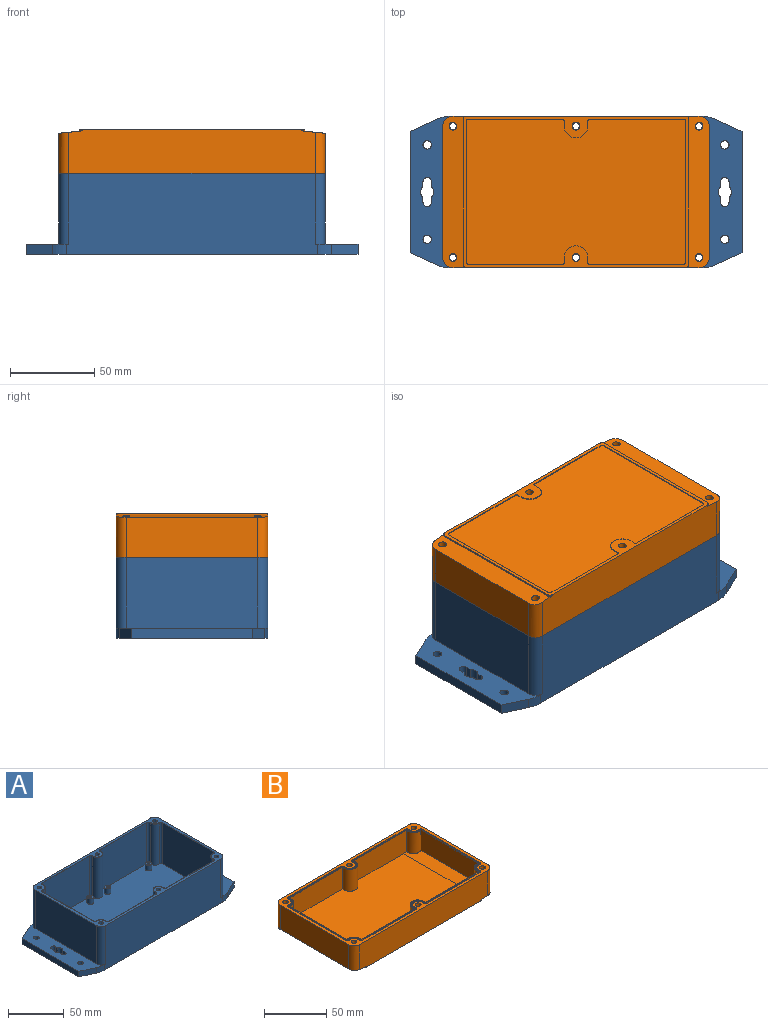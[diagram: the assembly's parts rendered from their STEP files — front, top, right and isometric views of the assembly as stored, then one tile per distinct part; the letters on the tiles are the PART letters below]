
ASSEMBLY  parts=2 mates=1
PART A: 174 faces, bbox 197x90x48.2 mm
  f0: plane 152x84mm, normal (0,0,1), area 12104mm2, adj f98,f99,f100,f101,f102,f103,f104,f106
  f1: plane 158x90mm, normal (0,0,1), area 1628.3mm2, adj f4,f6,f7,f8,f35,f38,f41,f44
  f2: plane 90x25.5mm, normal (0,0,1), area 1458.8mm2, adj f4,f7,f8,f22,f23,f24,f25,f26
  f3: plane 197x90mm, normal (0,0,-1), area 16841.5mm2, adj f7,f8,f9,f10,f11,f12,f13,f14
  f4: plane 78x42mm, normal (1,0,0), area 3276mm2, adj f1,f2,f168,f169
  f5: plane 90x25.5mm, normal (0,0,1), area 1458.8mm2, adj f6,f7,f8,f9,f10,f11,f12,f13
  f6: plane 78x42mm, normal (-1,0,0), area 3276mm2, adj f1,f5,f166,f167
  f7: plane 149.21x48mm, normal (0,-1,0), area 7027.3mm2, adj f1,f2,f3,f5,f167,f168,f171,f173
  f8: plane 149.21x48mm, normal (0,1,0), area 7027.3mm2, adj f1,f2,f3,f5,f166,f169,f170,f172
  f9: plane 15.51x7.16mm, normal (-0.42,0.91,0), area 102.5mm2, adj f3,f5,f10,f172
  f10: plane 72x6mm, normal (-1,0,0), area 432mm2, adj f3,f5,f9,f11
  f11: plane 15.51x7.16mm, normal (-0.42,-0.91,0), area 102.5mm2, adj f3,f5,f10,f173
  f12: cylinder r=2.5mm len=6mm, axis (0,0,1), area 94.2mm2, adj f3,f5
  f13: cylinder r=2.5mm len=6mm, axis (0,0,1), area 94.2mm2, adj f3,f5
  f14: cylinder r=4mm len=6.25mm, axis (0,0,1), area 43mm2, adj f3,f5,f15,f21
  f15: plane 6x3.03mm, normal (1,0,0), area 18.2mm2, adj f3,f5,f14,f16
  f16: cylinder r=2.5mm len=6mm, axis (0,0,1), area 47.1mm2, adj f3,f5,f15,f17
  f17: plane 6x3.03mm, normal (-1,0,0), area 18.2mm2, adj f3,f5,f16,f18
  f18: cylinder r=4mm len=6.25mm, axis (0,0,1), area 43mm2, adj f3,f5,f17,f19
  f19: plane 6x3.03mm, normal (-1,0,0), area 18.2mm2, adj f3,f5,f18,f20
  f20: cylinder r=2.5mm len=6mm, axis (0,0,1), area 47.1mm2, adj f3,f5,f19,f21
  f21: plane 6x3.03mm, normal (1,0,0), area 18.2mm2, adj f3,f5,f14,f20
  f22: plane 15.51x7.16mm, normal (0.42,-0.91,0), area 102.5mm2, adj f2,f3,f23,f171
  f23: plane 72x6mm, normal (1,0,0), area 432mm2, adj f2,f3,f22,f24
  f24: plane 15.51x7.16mm, normal (0.42,0.91,0), area 102.5mm2, adj f2,f3,f23,f170
  f25: cylinder r=2.5mm len=6mm, axis (0,0,1), area 94.2mm2, adj f2,f3
  f26: cylinder r=2.5mm len=6mm, axis (0,0,1), area 94.2mm2, adj f2,f3
  f27: cylinder r=4mm len=6.25mm, axis (0,0,1), area 43mm2, adj f2,f3,f28,f34
  f28: plane 6x3.03mm, normal (-1,0,0), area 18.2mm2, adj f2,f3,f27,f29
  f29: cylinder r=2.5mm len=6mm, axis (0,0,1), area 47.1mm2, adj f2,f3,f28,f30
  f30: plane 6x3.03mm, normal (1,0,0), area 18.2mm2, adj f2,f3,f29,f31
  f31: cylinder r=4mm len=6.25mm, axis (0,0,1), area 43mm2, adj f2,f3,f30,f32
  f32: plane 6x3.03mm, normal (1,0,0), area 18.2mm2, adj f2,f3,f31,f33
  f33: cylinder r=2.5mm len=6mm, axis (0,0,1), area 47.1mm2, adj f2,f3,f32,f34
  f34: plane 6x3.03mm, normal (-1,0,0), area 18.2mm2, adj f2,f3,f27,f33
  f35: cylinder r=2mm len=6mm, axis (0,0,-1), area 75.4mm2, adj f1,f36
  f36: plane 7.5x7.5mm, normal (0,0,-1), area 31.6mm2, adj f35,f37
  f37: cylinder r=3.75mm len=42mm, axis (0,0,-1), area 989.6mm2, adj f3,f36
  f38: cylinder r=2mm len=6mm, axis (0,0,-1), area 75.4mm2, adj f1,f39
  f39: plane 7.5x7.5mm, normal (0,0,-1), area 31.6mm2, adj f38,f40
  f40: cylinder r=3.75mm len=42mm, axis (0,0,-1), area 989.6mm2, adj f3,f39
  f41: cylinder r=2mm len=6mm, axis (0,0,-1), area 75.4mm2, adj f1,f42
  f42: plane 7.5x7.5mm, normal (0,0,-1), area 31.6mm2, adj f41,f43
  f43: cylinder r=3.75mm len=42mm, axis (0,0,-1), area 989.6mm2, adj f3,f42
  f44: cylinder r=2mm len=6mm, axis (0,0,-1), area 75.4mm2, adj f1,f45
  f45: plane 7.5x7.5mm, normal (0,0,-1), area 31.6mm2, adj f44,f46
  f46: cylinder r=3.75mm len=42mm, axis (0,0,-1), area 989.6mm2, adj f3,f45
  f47: cylinder r=2mm len=6mm, axis (0,0,-1), area 75.4mm2, adj f1,f48
  f48: plane 7.5x7.5mm, normal (0,0,-1), area 31.6mm2, adj f47,f49
  f49: cylinder r=3.75mm len=42mm, axis (0,0,-1), area 989.6mm2, adj f3,f48
  f50: cylinder r=2mm len=6mm, axis (0,0,-1), area 75.4mm2, adj f1,f51
  f51: plane 7.5x7.5mm, normal (0,0,-1), area 31.6mm2, adj f50,f52
  f52: cylinder r=3.75mm len=42mm, axis (0,0,-1), area 989.6mm2, adj f3,f51
  f53: plane 152.4x84.4mm, normal (0,0,1), area 95.5mm2, adj f54,f55,f56,f57,f58,f59,f60,f61
  f54: cylinder r=2.2mm len=2.2mm, axis (0,0,-1), area 0.7mm2, adj f1,f53,f55,f85
  f55: plane 59.14x0.2mm, normal (0,1,0), area 11.8mm2, adj f1,f53,f54,f56
  f56: cylinder r=2.2mm len=2.51mm, axis (0,0,-1), area 0.8mm2, adj f1,f53,f55,f57
  f57: cylinder r=4.8mm len=9.6mm, axis (0,0,-1), area 3.3mm2, adj f1,f53,f56,f58
  f58: cylinder r=2.2mm len=2.51mm, axis (0,0,-1), area 0.8mm2, adj f1,f53,f57,f59
  f59: plane 59.14x0.2mm, normal (0,1,0), area 11.8mm2, adj f1,f53,f58,f60
  f60: cylinder r=2.2mm len=2.2mm, axis (0,0,-1), area 0.7mm2, adj f1,f53,f59,f61
  f61: plane 0.93x0.2mm, normal (-1,0,0), area 0.2mm2, adj f1,f53,f60,f62
  f62: cylinder r=4.8mm len=4.8mm, axis (0,0,-1), area 1.5mm2, adj f1,f53,f61,f63
  f63: plane 0.93x0.2mm, normal (0,1,0), area 0.2mm2, adj f1,f53,f62,f64
  f64: cylinder r=2.2mm len=2.2mm, axis (0,0,-1), area 0.7mm2, adj f1,f53,f63,f65
  f65: plane 64.14x0.2mm, normal (-1,0,0), area 12.8mm2, adj f1,f53,f64,f66
  f66: cylinder r=2.2mm len=2.2mm, axis (0,0,-1), area 0.7mm2, adj f1,f53,f65,f67
  f67: plane 0.93x0.2mm, normal (0,-1,0), area 0.2mm2, adj f1,f53,f66,f68
  f68: cylinder r=4.8mm len=4.8mm, axis (0,0,-1), area 1.5mm2, adj f1,f53,f67,f69
  f69: plane 0.93x0.2mm, normal (-1,0,0), area 0.2mm2, adj f1,f53,f68,f70
  f70: cylinder r=2.2mm len=2.2mm, axis (0,0,-1), area 0.7mm2, adj f1,f53,f69,f71
  f71: plane 59.14x0.2mm, normal (0,-1,0), area 11.8mm2, adj f1,f53,f70,f72
  f72: cylinder r=2.2mm len=2.51mm, axis (0,0,-1), area 0.8mm2, adj f1,f53,f71,f73
  f73: cylinder r=4.8mm len=9.6mm, axis (0,0,-1), area 3.3mm2, adj f1,f53,f72,f74
  f74: cylinder r=2.2mm len=2.51mm, axis (0,0,-1), area 0.8mm2, adj f1,f53,f73,f75
  f75: plane 59.14x0.2mm, normal (0,-1,0), area 11.8mm2, adj f1,f53,f74,f76
  f76: cylinder r=2.2mm len=2.2mm, axis (0,0,-1), area 0.7mm2, adj f1,f53,f75,f77
  f77: plane 0.93x0.2mm, normal (1,0,0), area 0.2mm2, adj f1,f53,f76,f78
  f78: cylinder r=4.8mm len=4.8mm, axis (0,0,-1), area 1.5mm2, adj f1,f53,f77,f79
  f79: plane 0.93x0.2mm, normal (0,-1,0), area 0.2mm2, adj f1,f53,f78,f80
  f80: cylinder r=2.2mm len=2.2mm, axis (0,0,-1), area 0.7mm2, adj f1,f53,f79,f81
  f81: plane 64.14x0.2mm, normal (1,0,0), area 12.8mm2, adj f1,f53,f80,f82
  f82: cylinder r=2.2mm len=2.2mm, axis (0,0,-1), area 0.7mm2, adj f1,f53,f81,f83
  f83: plane 0.93x0.2mm, normal (0,1,0), area 0.2mm2, adj f1,f53,f82,f84
  f84: cylinder r=4.8mm len=4.8mm, axis (0,0,-1), area 1.5mm2, adj f1,f53,f83,f85
  f85: plane 0.93x0.2mm, normal (1,0,0), area 0.2mm2, adj f1,f53,f54,f84
  f86: plane 0.93x0.2mm, normal (1,0,0), area 0.2mm2, adj f53,f87,f119,f120
  f87: cylinder r=5mm len=5mm, axis (0,0,-1), area 1.6mm2, adj f53,f86,f88,f120
  f88: plane 0.93x0.2mm, normal (0,-1,0), area 0.2mm2, adj f53,f87,f102,f120
  f89: plane 0.93x0.2mm, normal (0,1,0), area 0.2mm2, adj f53,f90,f116,f117
  f90: cylinder r=5mm len=5mm, axis (0,0,-1), area 1.6mm2, adj f53,f89,f91,f117
  f91: plane 0.93x0.2mm, normal (1,0,0), area 0.2mm2, adj f53,f90,f114,f117
  f92: plane 0.93x0.2mm, normal (-1,0,0), area 0.2mm2, adj f53,f93,f108,f109
  f93: cylinder r=5mm len=5mm, axis (0,0,-1), area 1.6mm2, adj f53,f92,f94,f109
  f94: plane 0.93x0.2mm, normal (0,1,0), area 0.2mm2, adj f53,f93,f106,f109
  f95: plane 0.93x0.2mm, normal (0,-1,0), area 0.2mm2, adj f53,f96,f104,f105
  f96: cylinder r=5mm len=5mm, axis (0,0,-1), area 1.6mm2, adj f53,f95,f97,f105
  f97: plane 0.93x0.2mm, normal (-1,0,0), area 0.2mm2, adj f53,f96,f103,f105
  f98: cylinder r=5mm len=45mm, axis (0,0,-1), area 417.9mm2, adj f0,f114,f116,f117
  f99: cylinder r=5mm len=45mm, axis (0,0,-1), area 417.9mm2, adj f0,f106,f108,f109
  f100: cylinder r=5mm len=45mm, axis (0,0,-1), area 417.9mm2, adj f0,f103,f104,f105
  f101: cylinder r=5mm len=45mm, axis (0,0,-1), area 417.9mm2, adj f0,f102,f119,f120
  f102: cylinder r=2mm len=45.2mm, axis (0,0,-1), area 154.9mm2, adj f0,f53,f88,f101,f118,f120
  f103: cylinder r=2mm len=45.2mm, axis (0,0,-1), area 154.9mm2, adj f0,f53,f97,f100,f105,f125
  f104: cylinder r=2mm len=45.2mm, axis (0,0,-1), area 154.9mm2, adj f0,f53,f95,f100,f105,f107
  f105: plane 6x6mm, normal (0,0,1), area 0.8mm2, adj f95,f96,f97,f100,f103,f104
  f106: cylinder r=2mm len=45.2mm, axis (0,0,-1), area 154.9mm2, adj f0,f53,f94,f99,f107,f109
  f107: plane 64.14x45.2mm, normal (-1,0,0), area 2899.3mm2, adj f0,f53,f104,f106
  f108: cylinder r=2mm len=45.2mm, axis (0,0,-1), area 154.9mm2, adj f0,f53,f92,f99,f109,f113
  f109: plane 6x6mm, normal (0,0,1), area 0.8mm2, adj f92,f93,f94,f99,f106,f108
  f110: cylinder r=2mm len=45.2mm, axis (0,0,-1), area 155mm2, adj f0,f53,f112,f113
  f111: cylinder r=2mm len=45.2mm, axis (0,0,-1), area 155mm2, adj f0,f53,f112,f115
  f112: cylinder r=5mm len=45.2mm, axis (0,0,-1), area 774.8mm2, adj f0,f53,f110,f111
  f113: plane 59.14x45.2mm, normal (0,1,0), area 2673.3mm2, adj f0,f53,f108,f110
  f114: cylinder r=2mm len=45.2mm, axis (0,0,-1), area 154.9mm2, adj f0,f53,f91,f98,f115,f117
  f115: plane 59.14x45.2mm, normal (0,1,0), area 2673.3mm2, adj f0,f53,f111,f114
  f116: cylinder r=2mm len=45.2mm, axis (0,0,-1), area 154.9mm2, adj f0,f53,f89,f98,f117,f118
  f117: plane 6x6mm, normal (0,0,1), area 0.8mm2, adj f89,f90,f91,f98,f114,f116
  f118: plane 64.14x45.2mm, normal (1,0,0), area 2899.3mm2, adj f0,f53,f102,f116
  f119: cylinder r=2mm len=45.2mm, axis (0,0,-1), area 154.9mm2, adj f0,f53,f86,f101,f120,f124
  f120: plane 6x6mm, normal (0,0,1), area 0.8mm2, adj f86,f87,f88,f101,f102,f119
  f121: cylinder r=2mm len=45.2mm, axis (0,0,-1), area 155mm2, adj f0,f53,f123,f125
  f122: cylinder r=2mm len=45.2mm, axis (0,0,-1), area 155mm2, adj f0,f53,f123,f124
  f123: cylinder r=5mm len=45.2mm, axis (0,0,-1), area 774.8mm2, adj f0,f53,f121,f122
  f124: plane 59.14x45.2mm, normal (0,-1,0), area 2673.3mm2, adj f0,f53,f119,f122
  f125: plane 59.14x45.2mm, normal (0,-1,0), area 2673.3mm2, adj f0,f53,f103,f121
  f126: cylinder r=3mm len=6mm, axis (0,0,-1), area 113.1mm2, adj f0,f127
  f127: plane 6x6mm, normal (0,0,1), area 23.4mm2, adj f126,f165
  f128: cylinder r=3mm len=6mm, axis (0,0,-1), area 113.1mm2, adj f0,f129
  f129: plane 6x6mm, normal (0,0,1), area 23.4mm2, adj f128,f163
  f130: cylinder r=3mm len=6mm, axis (0,0,-1), area 113.1mm2, adj f0,f131
  f131: plane 6x6mm, normal (0,0,1), area 23.4mm2, adj f130,f159
  f132: cylinder r=3mm len=6mm, axis (0,0,-1), area 113.1mm2, adj f0,f133
  f133: plane 6x6mm, normal (0,0,1), area 23.4mm2, adj f132,f161
  f134: cylinder r=3mm len=6mm, axis (0,0,-1), area 113.1mm2, adj f0,f135
  f135: plane 6x6mm, normal (0,0,1), area 23.4mm2, adj f134,f149
  f136: cylinder r=3mm len=6mm, axis (0,0,-1), area 113.1mm2, adj f0,f137
  f137: plane 6x6mm, normal (0,0,1), area 23.4mm2, adj f136,f147
  f138: cylinder r=3mm len=6mm, axis (0,0,-1), area 113.1mm2, adj f0,f139
  f139: plane 6x6mm, normal (0,0,1), area 23.4mm2, adj f138,f151
  f140: cylinder r=3mm len=6mm, axis (0,0,-1), area 113.1mm2, adj f0,f141
  f141: plane 6x6mm, normal (0,0,1), area 23.4mm2, adj f140,f153
  f142: cylinder r=3mm len=6mm, axis (0,0,-1), area 113.1mm2, adj f0,f143
  f143: plane 6x6mm, normal (0,0,1), area 23.4mm2, adj f142,f155
  f144: cylinder r=3mm len=6mm, axis (0,0,-1), area 113.1mm2, adj f0,f145
  f145: plane 6x6mm, normal (0,0,1), area 23.4mm2, adj f144,f157
  f146: plane 2.5x2.5mm, normal (0,0,1), area 4.9mm2, adj f147
  f147: cylinder r=1.25mm len=6mm, axis (0,0,1), area 47.1mm2, adj f137,f146
  f148: plane 2.5x2.5mm, normal (0,0,1), area 4.9mm2, adj f149
  f149: cylinder r=1.25mm len=6mm, axis (0,0,1), area 47.1mm2, adj f135,f148
  f150: plane 2.5x2.5mm, normal (0,0,1), area 4.9mm2, adj f151
  f151: cylinder r=1.25mm len=6mm, axis (0,0,1), area 47.1mm2, adj f139,f150
  f152: plane 2.5x2.5mm, normal (0,0,1), area 4.9mm2, adj f153
  f153: cylinder r=1.25mm len=6mm, axis (0,0,1), area 47.1mm2, adj f141,f152
  f154: plane 2.5x2.5mm, normal (0,0,1), area 4.9mm2, adj f155
  f155: cylinder r=1.25mm len=6mm, axis (0,0,1), area 47.1mm2, adj f143,f154
  f156: plane 2.5x2.5mm, normal (0,0,1), area 4.9mm2, adj f157
  f157: cylinder r=1.25mm len=6mm, axis (0,0,1), area 47.1mm2, adj f145,f156
  f158: plane 2.5x2.5mm, normal (0,0,1), area 4.9mm2, adj f159
  f159: cylinder r=1.25mm len=6mm, axis (0,0,1), area 47.1mm2, adj f131,f158
  f160: plane 2.5x2.5mm, normal (0,0,1), area 4.9mm2, adj f161
  f161: cylinder r=1.25mm len=6mm, axis (0,0,1), area 47.1mm2, adj f133,f160
  f162: plane 2.5x2.5mm, normal (0,0,1), area 4.9mm2, adj f163
  f163: cylinder r=1.25mm len=6mm, axis (0,0,1), area 47.1mm2, adj f129,f162
  f164: plane 2.5x2.5mm, normal (0,0,1), area 4.9mm2, adj f165
  f165: cylinder r=1.25mm len=6mm, axis (0,0,1), area 47.1mm2, adj f127,f164
  f166: cylinder r=6mm len=42mm, axis (0,0,-1), area 395.8mm2, adj f1,f5,f6,f8
  f167: cylinder r=6mm len=42mm, axis (0,0,-1), area 395.8mm2, adj f1,f5,f6,f7
  f168: cylinder r=6mm len=42mm, axis (0,0,-1), area 395.8mm2, adj f1,f2,f4,f7
  f169: cylinder r=6mm len=42mm, axis (0,0,-1), area 395.8mm2, adj f1,f2,f4,f8
  f170: cylinder r=20mm len=8.38mm, axis (0,0,-1), area 51.9mm2, adj f2,f3,f8,f24
  f171: cylinder r=20mm len=8.38mm, axis (0,0,-1), area 51.9mm2, adj f2,f3,f7,f22
  f172: cylinder r=20mm len=8.38mm, axis (0,0,1), area 51.9mm2, adj f3,f5,f8,f9
  f173: cylinder r=20mm len=8.38mm, axis (0,0,1), area 51.9mm2, adj f3,f5,f7,f11
PART B: 110 faces, bbox 158.1x90.1x26.1 mm
  f0: plane 158x90mm, normal (0,0,1), area 1469.4mm2, adj f1,f2,f3,f4,f5,f6,f8,f9
  f1: plane 78x23.84mm, normal (-1,0,0), area 1859.4mm2, adj f0,f2,f3,f11
  f2: cylinder r=6mm len=24.47mm, axis (0,0,-1), area 226.8mm2, adj f0,f1,f6,f11
  f3: cylinder r=6mm len=24.47mm, axis (0,0,-1), area 226.8mm2, adj f0,f1,f4,f11
  f4: plane 146x26mm, normal (0,-1,0), area 3778.2mm2, adj f0,f3,f7,f9,f11,f13,f15,f16
  f5: plane 78x23.84mm, normal (1,0,0), area 1859.4mm2, adj f0,f8,f9,f13
  f6: plane 146x26mm, normal (0,1,0), area 3778.2mm2, adj f0,f2,f7,f8,f11,f13,f14,f17
  f7: plane 134x90mm, normal (0,0,-1), area 1111mm2, adj f4,f6,f10,f12,f14,f15,f16,f17
  f8: cylinder r=6mm len=24.47mm, axis (0,0,-1), area 226.8mm2, adj f0,f5,f6,f13
  f9: cylinder r=6mm len=24.47mm, axis (0,0,-1), area 226.8mm2, adj f0,f4,f5,f13
  f10: plane 86x0.9mm, normal (-1,0,0), area 77.4mm2, adj f7,f11,f16,f17
  f11: plane 90.1x14.1mm, normal (-0.1,0,-0.99), area 1038.7mm2, adj f1,f2,f3,f4,f6,f10,f16,f17
  f12: plane 86x0.9mm, normal (1,0,0), area 77.4mm2, adj f7,f13,f14,f15
  f13: plane 90.1x14.1mm, normal (0.1,0,-0.99), area 1038.7mm2, adj f4,f5,f6,f8,f9,f12,f14,f15
  f14: cylinder r=2mm len=2mm, axis (0,0,-1), area 2.5mm2, adj f6,f7,f12,f13
  f15: cylinder r=2mm len=2mm, axis (0,0,-1), area 2.5mm2, adj f4,f7,f12,f13
  f16: cylinder r=2mm len=2mm, axis (0,0,-1), area 2.5mm2, adj f4,f7,f10,f11
  f17: cylinder r=2mm len=2mm, axis (0,0,-1), area 2.5mm2, adj f6,f7,f10,f11
  f18: cylinder r=2.3mm len=24.71mm, axis (0,0,-1), area 353.5mm2, adj f0,f11
  f19: cylinder r=2.3mm len=24.71mm, axis (0,0,-1), area 353.5mm2, adj f0,f11
  f20: cylinder r=2.3mm len=24.71mm, axis (0,0,-1), area 353.5mm2, adj f0,f13
  f21: cylinder r=2.3mm len=24.71mm, axis (0,0,-1), area 353.5mm2, adj f0,f13
  f22: cylinder r=2.3mm len=26mm, axis (0,0,-1), area 375.7mm2, adj f0,f7
  f23: cylinder r=2.3mm len=26mm, axis (0,0,-1), area 375.7mm2, adj f0,f7
  f24: cylinder r=7mm len=14mm, axis (0,0,-1), area 11mm2, adj f7,f25,f43,f44
  f25: plane 3x0.5mm, normal (1,0,0), area 1.5mm2, adj f7,f24,f26,f44
  f26: cylinder r=1mm len=1mm, axis (0,0,-1), area 0.8mm2, adj f7,f25,f27,f44
  f27: plane 56x0.5mm, normal (0,1,0), area 28mm2, adj f7,f26,f28,f44
  f28: cylinder r=1mm len=1mm, axis (0,0,-1), area 0.8mm2, adj f7,f27,f29,f44
  f29: plane 84x0.5mm, normal (-1,0,0), area 42mm2, adj f7,f28,f30,f44
  f30: cylinder r=1mm len=1mm, axis (0,0,-1), area 0.8mm2, adj f7,f29,f31,f44
  f31: plane 56x0.5mm, normal (0,-1,0), area 28mm2, adj f7,f30,f32,f44
  f32: cylinder r=1mm len=1mm, axis (0,0,-1), area 0.8mm2, adj f7,f31,f33,f44
  f33: plane 3x0.5mm, normal (1,0,0), area 1.5mm2, adj f7,f32,f34,f44
  f34: cylinder r=7mm len=14mm, axis (0,0,-1), area 11mm2, adj f7,f33,f35,f44
  f35: plane 3x0.5mm, normal (-1,0,0), area 1.5mm2, adj f7,f34,f36,f44
  f36: cylinder r=1mm len=1mm, axis (0,0,-1), area 0.8mm2, adj f7,f35,f37,f44
  f37: plane 56x0.5mm, normal (0,-1,0), area 28mm2, adj f7,f36,f38,f44
  f38: cylinder r=1mm len=1mm, axis (0,0,-1), area 0.8mm2, adj f7,f37,f39,f44
  f39: plane 84x0.5mm, normal (1,0,0), area 42mm2, adj f7,f38,f40,f44
  f40: cylinder r=1mm len=1mm, axis (0,0,-1), area 0.8mm2, adj f7,f39,f41,f44
  f41: plane 56x0.5mm, normal (0,1,0), area 28mm2, adj f7,f40,f42,f44
  f42: cylinder r=1mm len=1mm, axis (0,0,-1), area 0.8mm2, adj f7,f41,f43,f44
  f43: plane 3x0.5mm, normal (-1,0,0), area 1.5mm2, adj f7,f24,f42,f44
  f44: plane 130x86mm, normal (0,0,-1), area 10912.3mm2, adj f24,f25,f26,f27,f28,f29,f30,f31
  f45: cylinder r=2mm len=2.45mm, axis (0,0,1), area 3.6mm2, adj f0,f46,f68,f69
  f46: cylinder r=4.65mm len=5.7mm, axis (0,0,1), area 9.4mm2, adj f0,f45,f47,f69
  f47: cylinder r=2mm len=2.45mm, axis (0,0,1), area 3.6mm2, adj f0,f46,f48,f69
  f48: plane 65.04x1mm, normal (1,0,0), area 65mm2, adj f0,f47,f49,f69
  f49: cylinder r=2mm len=2.45mm, axis (0,0,1), area 3.6mm2, adj f0,f48,f50,f69
  f50: cylinder r=4.65mm len=5.7mm, axis (0,0,1), area 9.4mm2, adj f0,f49,f51,f69
  f51: cylinder r=2mm len=2.45mm, axis (0,0,1), area 3.6mm2, adj f0,f50,f52,f69
  f52: plane 60.04x1mm, normal (0,-1,0), area 60mm2, adj f0,f51,f53,f69
  f53: cylinder r=2mm len=2.45mm, axis (0,0,1), area 3.6mm2, adj f0,f52,f54,f69
  f54: cylinder r=4.65mm len=9.3mm, axis (0,0,1), area 16.7mm2, adj f0,f53,f55,f69
  f55: cylinder r=2mm len=2.45mm, axis (0,0,1), area 3.6mm2, adj f0,f54,f56,f69
  f56: plane 60.04x1mm, normal (0,-1,0), area 60mm2, adj f0,f55,f57,f69
  f57: cylinder r=2mm len=2.45mm, axis (0,0,1), area 3.6mm2, adj f0,f56,f58,f69
  f58: cylinder r=4.65mm len=5.7mm, axis (0,0,1), area 9.4mm2, adj f0,f57,f59,f69
  f59: cylinder r=2mm len=2.45mm, axis (0,0,1), area 3.6mm2, adj f0,f58,f60,f69
  f60: plane 65.04x1mm, normal (-1,0,0), area 65mm2, adj f0,f59,f61,f69
  f61: cylinder r=2mm len=2.45mm, axis (0,0,1), area 3.6mm2, adj f0,f60,f62,f69
  f62: cylinder r=4.65mm len=5.7mm, axis (0,0,1), area 9.4mm2, adj f0,f61,f63,f69
  f63: cylinder r=2mm len=2.45mm, axis (0,0,1), area 3.6mm2, adj f0,f62,f64,f69
  f64: plane 60.04x1mm, normal (0,1,0), area 60mm2, adj f0,f63,f65,f69
  f65: cylinder r=2mm len=2.45mm, axis (0,0,1), area 3.6mm2, adj f0,f64,f66,f69
  f66: cylinder r=4.65mm len=9.3mm, axis (0,0,1), area 16.7mm2, adj f0,f65,f67,f69
  f67: cylinder r=2mm len=2.45mm, axis (0,0,1), area 3.6mm2, adj f0,f66,f68,f69
  f68: plane 60.04x1mm, normal (0,1,0), area 60mm2, adj f0,f45,f67,f69
  f69: plane 153x85mm, normal (0,0,1), area 481.4mm2, adj f45,f46,f47,f48,f49,f50,f51,f52
  f70: cylinder r=1mm len=1.23mm, axis (0,0,1), area 1.8mm2, adj f69,f71,f93,f109
  f71: cylinder r=5.65mm len=6.92mm, axis (0,0,1), area 11.4mm2, adj f69,f70,f72,f109
  f72: cylinder r=1mm len=1.23mm, axis (0,0,1), area 1.8mm2, adj f69,f71,f73,f109
  f73: plane 65.04x1mm, normal (-1,0,0), area 65mm2, adj f69,f72,f74,f109
  f74: cylinder r=1mm len=1.23mm, axis (0,0,1), area 1.8mm2, adj f69,f73,f75,f109
  f75: cylinder r=5.65mm len=6.92mm, axis (0,0,1), area 11.4mm2, adj f69,f74,f76,f109
  f76: cylinder r=1mm len=1.23mm, axis (0,0,1), area 1.8mm2, adj f69,f75,f77,f109
  f77: plane 60.04x1mm, normal (0,1,0), area 60mm2, adj f69,f76,f78,f109
  f78: cylinder r=1mm len=1.23mm, axis (0,0,1), area 1.8mm2, adj f69,f77,f79,f109
  f79: cylinder r=5.65mm len=11.3mm, axis (0,0,1), area 20.3mm2, adj f69,f78,f80,f109
  f80: cylinder r=1mm len=1.23mm, axis (0,0,1), area 1.8mm2, adj f69,f79,f81,f109
  f81: plane 60.04x1mm, normal (0,1,0), area 60mm2, adj f69,f80,f82,f109
  f82: cylinder r=1mm len=1.23mm, axis (0,0,1), area 1.8mm2, adj f69,f81,f83,f109
  f83: cylinder r=5.65mm len=6.92mm, axis (0,0,1), area 11.4mm2, adj f69,f82,f84,f109
  f84: cylinder r=1mm len=1.23mm, axis (0,0,1), area 1.8mm2, adj f69,f83,f85,f109
  f85: plane 65.04x1mm, normal (1,0,0), area 65mm2, adj f69,f84,f86,f109
  f86: cylinder r=1mm len=1.23mm, axis (0,0,1), area 1.8mm2, adj f69,f85,f87,f109
  f87: cylinder r=5.65mm len=6.92mm, axis (0,0,1), area 11.4mm2, adj f69,f86,f88,f109
  f88: cylinder r=1mm len=1.23mm, axis (0,0,1), area 1.8mm2, adj f69,f87,f89,f109
  f89: plane 60.04x1mm, normal (0,-1,0), area 60mm2, adj f69,f88,f90,f109
  f90: cylinder r=1mm len=1.23mm, axis (0,0,1), area 1.8mm2, adj f69,f89,f91,f109
  f91: cylinder r=5.65mm len=11.3mm, axis (0,0,1), area 20.3mm2, adj f69,f90,f92,f109
  f92: cylinder r=1mm len=1.23mm, axis (0,0,1), area 1.8mm2, adj f69,f91,f93,f109
  f93: plane 60.04x1mm, normal (0,-1,0), area 60mm2, adj f69,f70,f92,f109
  f94: plane 81.6x11.83mm, normal (-0.1,0,0.99), area 850.6mm2, adj f95,f100,f101,f102,f103,f104
  f95: plane 125.95x81.6mm, normal (0,0,1), area 10098.5mm2, adj f94,f96,f98,f99,f100,f104,f105,f106
  f96: plane 81.6x11.83mm, normal (0.1,0,0.99), area 850.6mm2, adj f95,f97,f98,f106,f107,f108
  f97: cylinder r=6.5mm len=20.93mm, axis (0,0,-1), area 286.1mm2, adj f96,f98,f108,f109
  f98: plane 60.51x21.3mm, normal (0,1,0), area 1288.1mm2, adj f95,f96,f97,f99,f109
  f99: cylinder r=6.5mm len=21.3mm, axis (0,0,-1), area 512.6mm2, adj f95,f98,f100,f109
  f100: plane 60.51x21.3mm, normal (0,1,0), area 1288.1mm2, adj f94,f95,f99,f101,f109
  f101: cylinder r=6.5mm len=20.93mm, axis (0,0,-1), area 286.1mm2, adj f94,f100,f102,f109
  f102: plane 65.51x20.06mm, normal (-1,0,0), area 1313.9mm2, adj f94,f101,f103,f109
  f103: cylinder r=6.5mm len=20.93mm, axis (0,0,-1), area 286.1mm2, adj f94,f102,f104,f109
  f104: plane 60.51x21.3mm, normal (0,-1,0), area 1288.1mm2, adj f94,f95,f103,f105,f109
  f105: cylinder r=6.5mm len=21.3mm, axis (0,0,-1), area 512.6mm2, adj f95,f104,f106,f109
  f106: plane 60.51x21.3mm, normal (0,-1,0), area 1288.1mm2, adj f95,f96,f105,f107,f109
  f107: cylinder r=6.5mm len=20.93mm, axis (0,0,-1), area 286.1mm2, adj f96,f106,f108,f109
  f108: plane 65.51x20.06mm, normal (1,0,0), area 1313.9mm2, adj f96,f97,f107,f109
  f109: plane 151x83mm, normal (0,0,1), area 348.2mm2, adj f70,f71,f72,f73,f74,f75,f76,f77
PLACE A at identity fixed
PLACE B rot(axis=(1,0,0),180deg) t=(0,90,74)mm
MATE slider B.f3 <-> A.f38  axis (0,0,-1) through (6,84,48)mm
